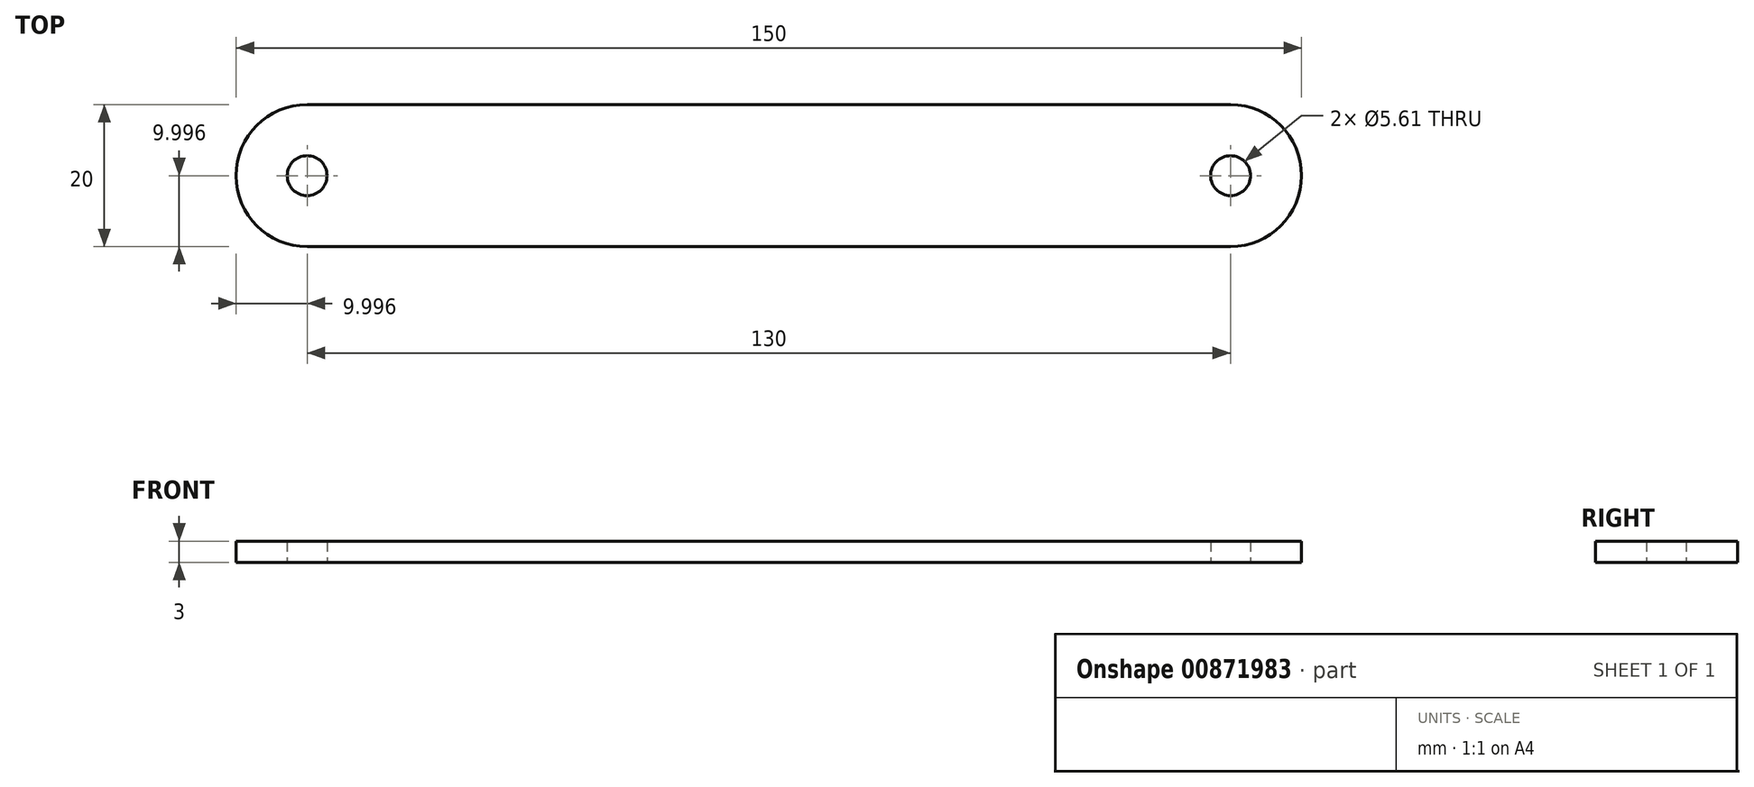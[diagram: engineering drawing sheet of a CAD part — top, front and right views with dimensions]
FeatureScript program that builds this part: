
annotation { "Feature Type Name" : "Feature", "Feature Type Description" : "" }
export const myFeature = defineFeature(function(context is Context, id is Id, definition is map)
    precondition{}
    {
        {
            var Q0;
            Q0=qCreatedBy(makeId("Top.planeOp"),FACE);
            var sketch = newSketch(context, id + "F0", { "sketchPlane" : qUnion([Q0])});
            skLineSegment(sketch, "E0.bottom", {"start": v(-15.54, 13.62) * mm, "end": v(114.46, 13.62) * mm});
            skLineSegment(sketch, "E0.top", {"start": v(-15.54, 33.62) * mm, "end": v(114.46, 33.62) * mm});
            skLineSegment(sketch, "E0.left", {"start": v(-15.54, 13.62) * mm, "end": v(-15.54, 33.62) * mm});
            skLineSegment(sketch, "E0.right", {"start": v(114.46, 13.62) * mm, "end": v(114.46, 33.62) * mm});
            skArc(sketch, "E1", {"start": v(-15.54, 13.62) * mm, "mid": v(-25.54, 23.62) * mm, "end": v(-15.54, 33.62) * mm});
            skArc(sketch, "E2", {"start": v(114.46, 33.62) * mm, "mid": v(124.46, 23.62) * mm, "end": v(114.46, 13.62) * mm});
            skCircle(sketch, "E3", {"center": v(-15.54, 23.62) * mm, "radius": 2.8 * mm});
            skCircle(sketch, "E4", {"center": v(114.46, 23.62) * mm, "radius": 2.8 * mm});
            skSolve(sketch);
        }
        {
            var Q0;
            Q0 = qSketchRegion(id + "F0", true);
            extrude(context, id + "F1", {"entities" : qUnion([Q0]), "depth" : 3 * mm, "offsetDistance" : 25.4 * mm});
        }
    });
